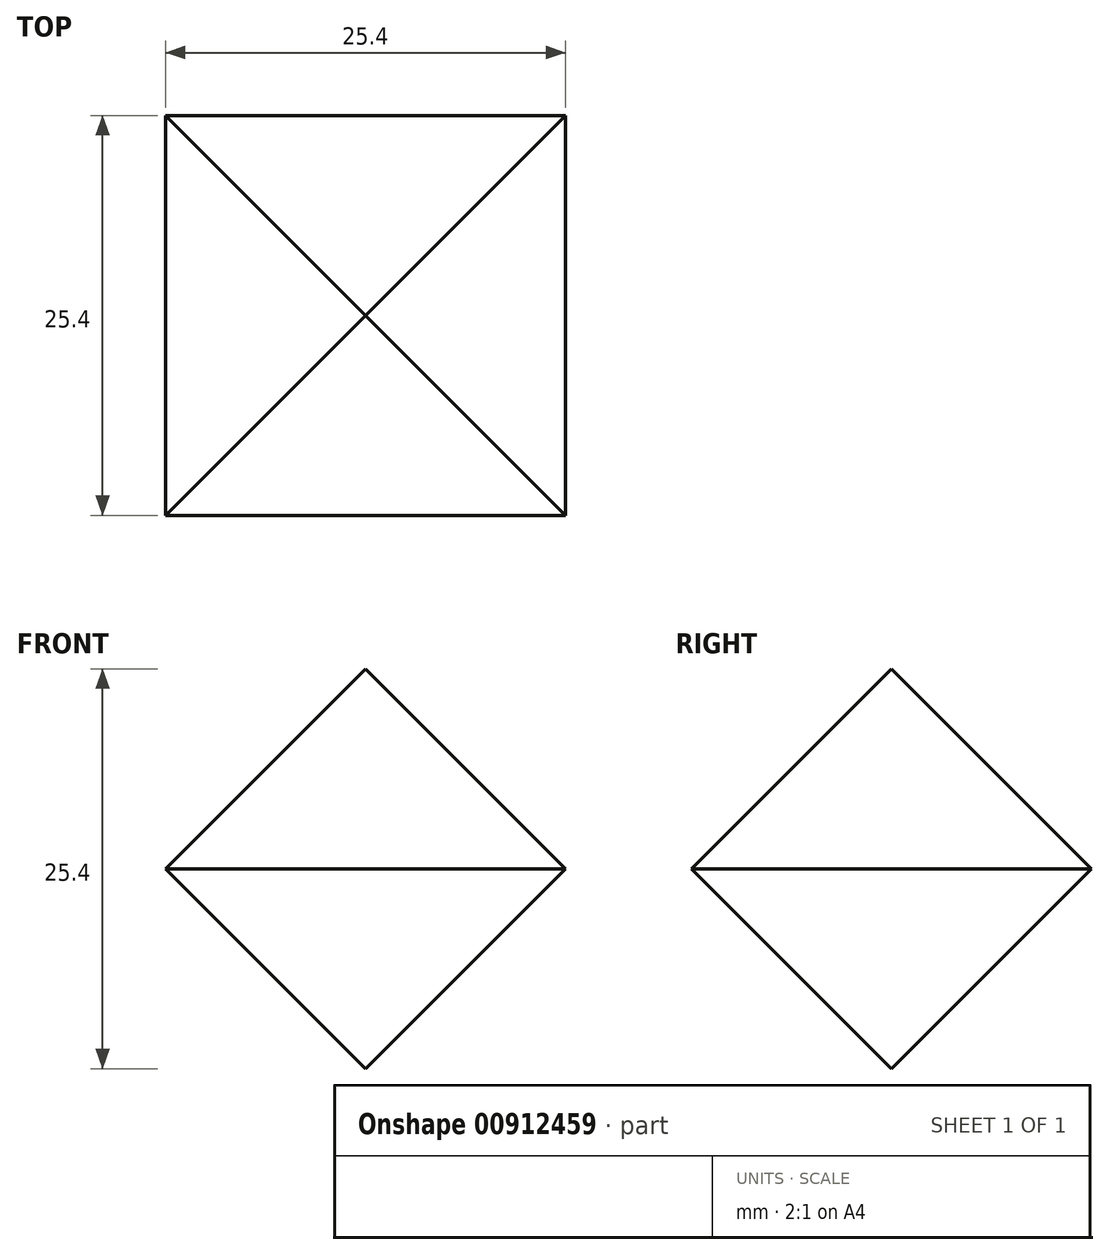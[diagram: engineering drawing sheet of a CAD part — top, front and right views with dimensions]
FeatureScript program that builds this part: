
annotation { "Feature Type Name" : "Feature", "Feature Type Description" : "" }
export const myFeature = defineFeature(function(context is Context, id is Id, definition is map)
    precondition{}
    {
        {
            var Q0;
            Q0=qCreatedBy(makeId("Front.planeOp"),FACE);
            var sketch = newSketch(context, id + "F0", { "sketchPlane" : qUnion([Q0])});
            skLineSegment(sketch, "E0", {"start": v(-35.18, 29.98) * mm, "end": v(-35.18, 4.58) * mm});
            skLineSegment(sketch, "E1", {"start": v(-35.18, 4.58) * mm, "end": v(-9.78, 4.58) * mm});
            skLineSegment(sketch, "E2", {"start": v(-9.78, 4.58) * mm, "end": v(-9.78, 29.98) * mm});
            skLineSegment(sketch, "E3", {"start": v(-9.78, 29.98) * mm, "end": v(-35.18, 29.98) * mm});
            skSolve(sketch);
        }
        {
            var Q0;
            Q0 = qSketchRegion(id + "F0", true);
            extrude(context, id + "F1", {"entities" : qUnion([Q0]), "depth" : 25.4 * mm, "offsetDistance" : 25.4 * mm});
        }
        {
            var Q0;
            Q0=makeQuery(id+"F1.opExtrude","CAP_FACE",FACE,{"disambiguationData":[OSD([sQuery(id+"F0.wireOp",EDGE,"E0"),sQuery(id+"F0.wireOp",EDGE,"E1"),sQuery(id+"F0.wireOp",EDGE,"E2"),sQuery(id+"F0.wireOp",EDGE,"E3")])],"isStart":false});
            var sketch = newSketch(context, id + "F2", { "sketchPlane" : qUnion([Q0])});
            skLineSegment(sketch, "E4", {"start": v(-22.48, 29.98) * mm, "end": v(-9.78, 17.28) * mm});
            skLineSegment(sketch, "E5", {"start": v(-9.78, 17.28) * mm, "end": v(-22.48, 4.58) * mm});
            skLineSegment(sketch, "E6", {"start": v(-22.48, 4.58) * mm, "end": v(-35.18, 17.28) * mm});
            skLineSegment(sketch, "E7", {"start": v(-35.18, 17.28) * mm, "end": v(-22.48, 29.98) * mm});
            skSolve(sketch);
        }
        {
            var Q0;
            Q0=makeQuery(id+"F1.opExtrude","SWEPT_FACE",FACE,{"disambiguationData":[OSD([sQuery(id+"F0.wireOp",EDGE,"E0")])]});
            var sketch = newSketch(context, id + "F3", { "sketchPlane" : qUnion([Q0])});
            skLineSegment(sketch, "E8", {"start": v(12.7, 29.98) * mm, "end": v(0, 17.28) * mm});
            skLineSegment(sketch, "E9", {"start": v(0, 17.28) * mm, "end": v(12.7, 4.58) * mm});
            skLineSegment(sketch, "E10", {"start": v(12.7, 4.58) * mm, "end": v(25.4, 17.28) * mm});
            skLineSegment(sketch, "E11", {"start": v(25.4, 17.28) * mm, "end": v(12.7, 29.98) * mm});
            skSolve(sketch);
        }
        {
            var Q0;
            {var subQ0=sQuery(id+"F3.wireOp",EDGE,"E11");Q0=makeQuery(id+"F3.imprint","IMPRINT",FACE,{"disambiguationData":[TD([[makeQuery(id+"F3.imprint","IMPRINT",EDGE,{"derivedFrom":subQ0}),-1.0]])]});}
            var Q1;
            {var subQ0=sQuery(id+"F3.wireOp",EDGE,"E8");Q1=makeQuery(id+"F3.imprint","IMPRINT",FACE,{"disambiguationData":[TD([[makeQuery(id+"F3.imprint","IMPRINT",EDGE,{"derivedFrom":subQ0}),-1.0]])]});}
            var Q2;
            {var subQ0=sQuery(id+"F3.wireOp",EDGE,"E9");Q2=makeQuery(id+"F3.imprint","IMPRINT",FACE,{"disambiguationData":[TD([[makeQuery(id+"F3.imprint","IMPRINT",EDGE,{"derivedFrom":subQ0}),-1.0]])]});}
            var Q3;
            {var subQ0=sQuery(id+"F3.wireOp",EDGE,"E10");Q3=makeQuery(id+"F3.imprint","IMPRINT",FACE,{"disambiguationData":[TD([[makeQuery(id+"F3.imprint","IMPRINT",EDGE,{"derivedFrom":subQ0}),-1.0]])]});}
            extrude(context, id + "F4", {"entities" : qUnion([Q0, Q1, Q2, Q3]), "operationType" : NewBodyOperationType.REMOVE, "oppositeDirection" : true, "depth" : 25.4 * mm, "offsetDistance" : 25.4 * mm});
        }
        {
            var Q0;
            {var subQ0=sQuery(id+"F2.wireOp",EDGE,"E4");Q0=makeQuery(id+"F2.imprint","IMPRINT",FACE,{"disambiguationData":[TD([[makeQuery(id+"F2.imprint","IMPRINT",EDGE,{"derivedFrom":subQ0}),1.0]])]});}
            var Q1;
            {var subQ0=sQuery(id+"F2.wireOp",EDGE,"E5");Q1=makeQuery(id+"F2.imprint","IMPRINT",FACE,{"disambiguationData":[TD([[makeQuery(id+"F2.imprint","IMPRINT",EDGE,{"derivedFrom":subQ0}),1.0]])]});}
            var Q2;
            {var subQ0=sQuery(id+"F2.wireOp",EDGE,"E6");Q2=makeQuery(id+"F2.imprint","IMPRINT",FACE,{"disambiguationData":[TD([[makeQuery(id+"F2.imprint","IMPRINT",EDGE,{"derivedFrom":subQ0}),1.0]])]});}
            var Q3;
            {var subQ0=sQuery(id+"F2.wireOp",EDGE,"E7");Q3=makeQuery(id+"F2.imprint","IMPRINT",FACE,{"disambiguationData":[TD([[makeQuery(id+"F2.imprint","IMPRINT",EDGE,{"derivedFrom":subQ0}),1.0]])]});}
            extrude(context, id + "F5", {"entities" : qUnion([Q0, Q1, Q2, Q3]), "operationType" : NewBodyOperationType.REMOVE, "oppositeDirection" : true, "depth" : 25.4 * mm, "offsetDistance" : 25.4 * mm});
        }
    });
